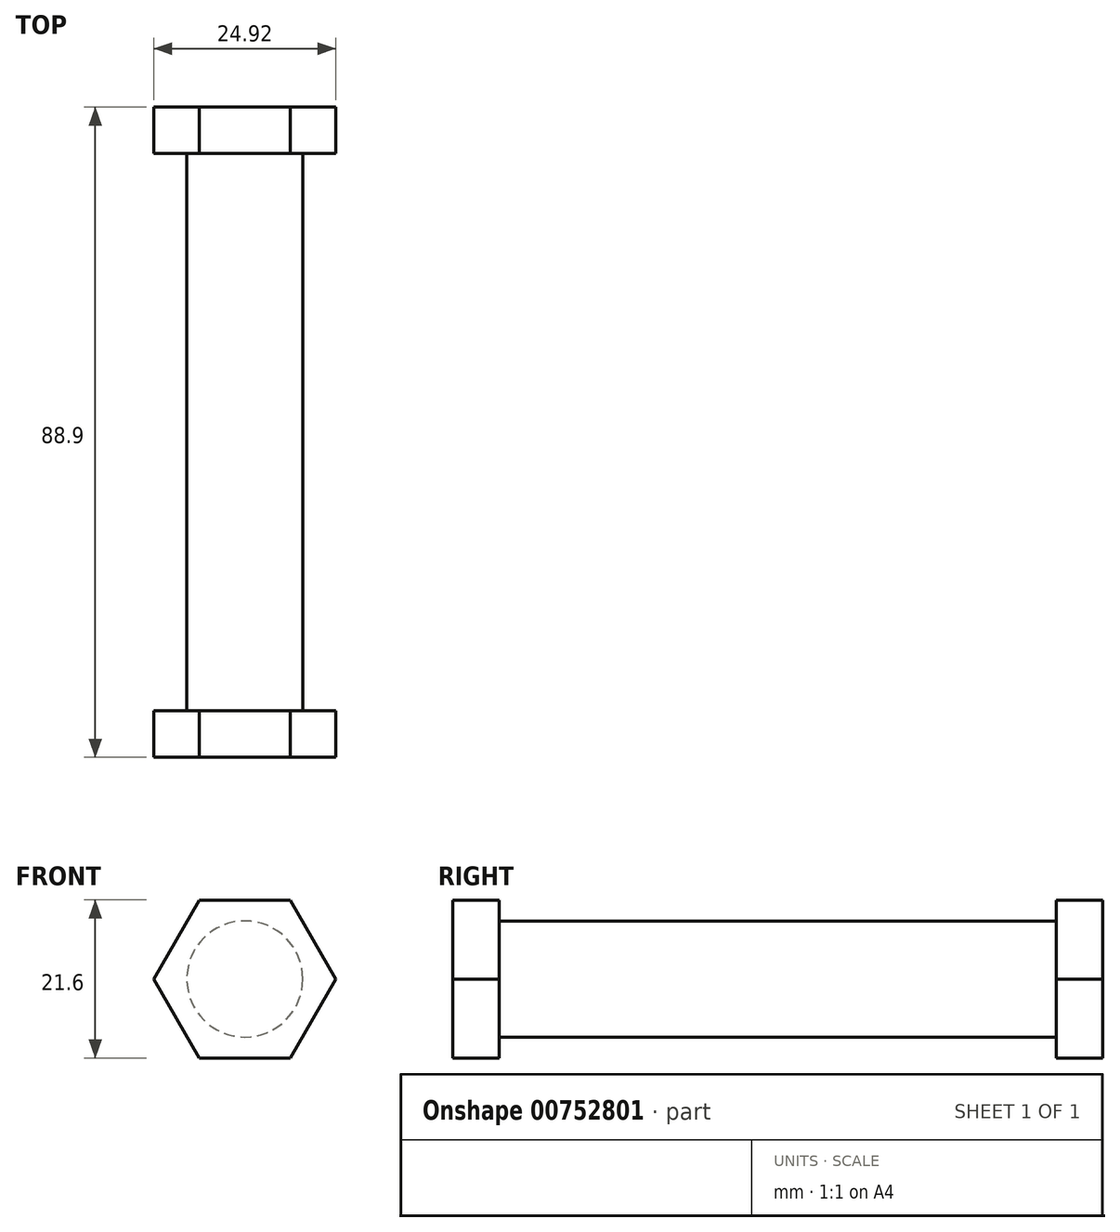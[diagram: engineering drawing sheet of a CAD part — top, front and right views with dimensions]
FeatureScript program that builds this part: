
annotation { "Feature Type Name" : "Feature", "Feature Type Description" : "" }
export const myFeature = defineFeature(function(context is Context, id is Id, definition is map)
    precondition{}
    {
        {
            var Q0;
            Q0=qCreatedBy(makeId("Front.planeOp"),FACE);
            var sketch = newSketch(context, id + "F0", { "sketchPlane" : qUnion([Q0])});
            skCircle(sketch, "E0.cCircle", {"center": v(0, 0) * mm, "radius": 10.8 * mm, "construction": true});
            skLineSegment(sketch, "E0.0", {"start": v(6.23, 10.8) * mm, "end": v(12.46, 0) * mm});
            skLineSegment(sketch, "E0.1", {"start": v(12.46, 0) * mm, "end": v(6.23, -10.8) * mm});
            skLineSegment(sketch, "E0.2", {"start": v(6.23, -10.8) * mm, "end": v(-6.23, -10.8) * mm});
            skLineSegment(sketch, "E0.3", {"start": v(-6.23, -10.8) * mm, "end": v(-12.46, 0) * mm});
            skLineSegment(sketch, "E0.4", {"start": v(-12.46, 0) * mm, "end": v(-6.23, 10.8) * mm});
            skLineSegment(sketch, "E0.5", {"start": v(-6.23, 10.8) * mm, "end": v(6.23, 10.8) * mm});
            skPoint(sketch, "E0.0.midPoint", {"position": v(9.35, 5.4) * mm});
            skSolve(sketch);
        }
        {
            var Q0;
            Q0=makeQuery(id+"F0.imprint","IMPRINT",FACE,{"disambiguationData":[TD([[makeQuery(id+"F0.imprint","IMPRINT",EDGE,{"derivedFrom":sQuery(id+"F0.wireOp",EDGE,"E0.0")}),-1.0]])]});
            extrude(context, id + "F1", {"entities" : qUnion([Q0]), "depth" : 6.35 * mm, "offsetDistance" : 25.4 * mm});
        }
        {
            var Q0;
            Q0=makeQuery(id+"F1.opExtrude","CAP_FACE",FACE,{"disambiguationData":[OSD([sQuery(id+"F0.wireOp",EDGE,"E0.0"),sQuery(id+"F0.wireOp",EDGE,"E0.1"),sQuery(id+"F0.wireOp",EDGE,"E0.2"),sQuery(id+"F0.wireOp",EDGE,"E0.3"),sQuery(id+"F0.wireOp",EDGE,"E0.4"),sQuery(id+"F0.wireOp",EDGE,"E0.5")])],"isStart":true});
            var sketch = newSketch(context, id + "F2", { "sketchPlane" : qUnion([Q0])});
            skCircle(sketch, "E1", {"center": v(0, 0) * mm, "radius": 7.94 * mm});
            skSolve(sketch);
        }
        {
            var Q0;
            Q0 = qSketchRegion(id + "F2", true);
            extrude(context, id + "F3", {"entities" : qUnion([Q0]), "operationType" : NewBodyOperationType.ADD, "depth" : 76.2 * mm, "offsetDistance" : 25.4 * mm});
        }
        {
            var Q0;
            Q0=makeQuery(id+"F3.opExtrude","CAP_FACE",FACE,{"disambiguationData":[OSD([sQuery(id+"F2.wireOp",EDGE,"E1")])],"isStart":false});
            var sketch = newSketch(context, id + "F4", { "sketchPlane" : qUnion([Q0])});
            skCircle(sketch, "E2.cCircle", {"center": v(0, 0) * mm, "radius": 10.8 * mm, "construction": true});
            skLineSegment(sketch, "E2.0", {"start": v(6.23, 10.8) * mm, "end": v(12.46, 0) * mm});
            skLineSegment(sketch, "E2.1", {"start": v(12.46, 0) * mm, "end": v(6.23, -10.8) * mm});
            skLineSegment(sketch, "E2.2", {"start": v(6.23, -10.8) * mm, "end": v(-6.23, -10.8) * mm});
            skLineSegment(sketch, "E2.3", {"start": v(-6.23, -10.8) * mm, "end": v(-12.46, 0) * mm});
            skLineSegment(sketch, "E2.4", {"start": v(-12.46, 0) * mm, "end": v(-6.23, 10.8) * mm});
            skLineSegment(sketch, "E2.5", {"start": v(-6.23, 10.8) * mm, "end": v(6.23, 10.8) * mm});
            skPoint(sketch, "E2.0.midPoint", {"position": v(9.35, 5.4) * mm});
            skSolve(sketch);
        }
        {
            var Q0;
            Q0=makeQuery(id+"F4.imprint","IMPRINT",FACE,{"disambiguationData":[TD([[makeQuery(id+"F4.imprint","IMPRINT",EDGE,{"derivedFrom":sQuery(id+"F4.wireOp",EDGE,"E2.0")}),-1.0]])]});
            var Q1;
            Q1=makeQuery(id+"F4.imprint","IMPRINT",FACE,{"disambiguationData":[TD([[makeQuery(id+"F4.imprint","IMPRINT",EDGE,{"derivedFrom":makeQuery(id+"F3.opExtrude","CAP_EDGE",EDGE,{"disambiguationData":[OSD([sQuery(id+"F2.wireOp",EDGE,"E1")])],"isStart":false})}),1.0]])]});
            extrude(context, id + "F5", {"entities" : qUnion([Q0, Q1]), "operationType" : NewBodyOperationType.ADD, "depth" : 6.35 * mm, "offsetDistance" : 25.4 * mm});
        }
    });
